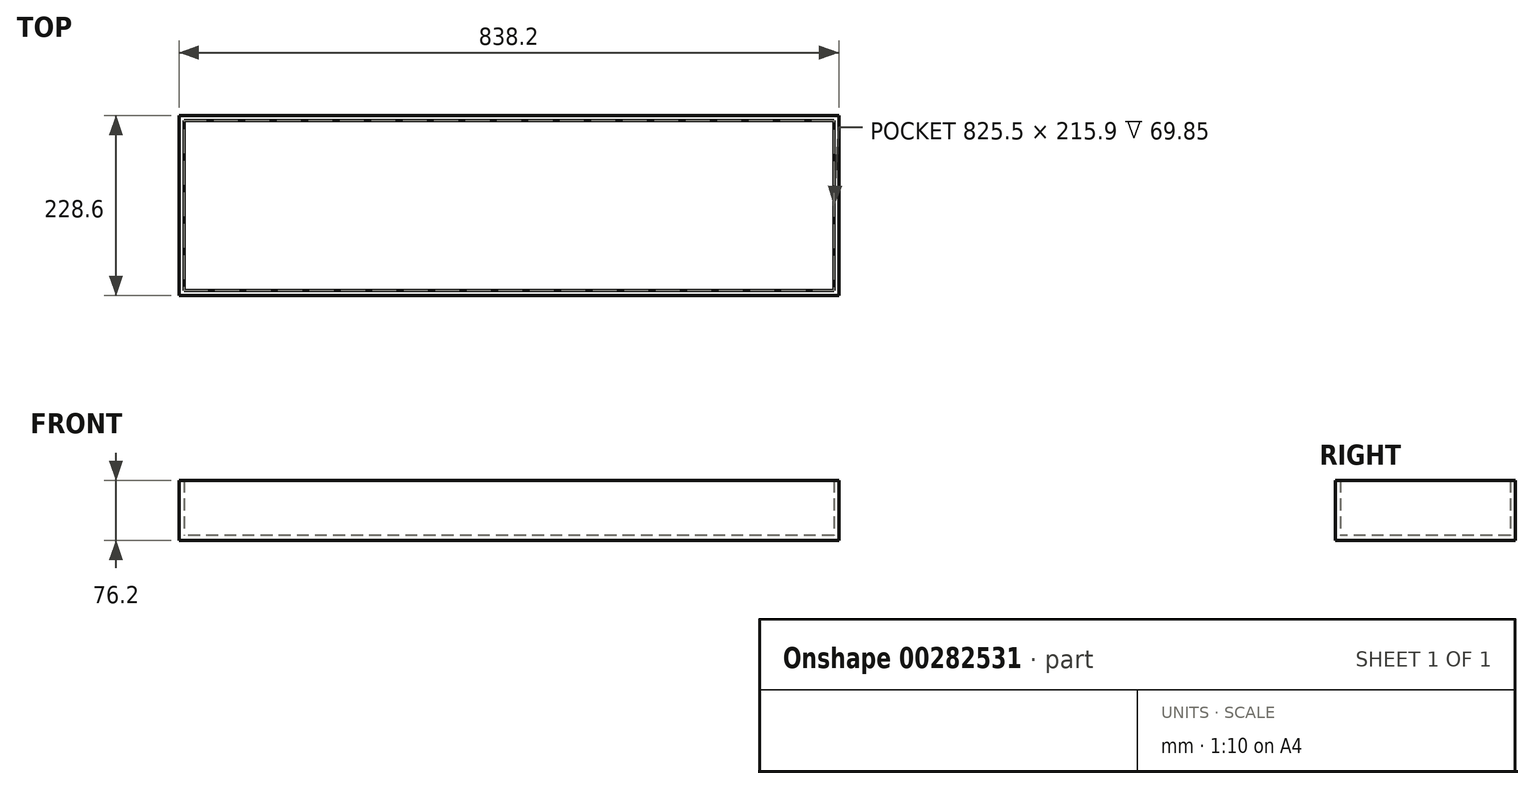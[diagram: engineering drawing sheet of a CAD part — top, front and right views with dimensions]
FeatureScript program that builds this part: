
annotation { "Feature Type Name" : "Feature", "Feature Type Description" : "" }
export const myFeature = defineFeature(function(context is Context, id is Id, definition is map)
    precondition{}
    {
        {
            var Q0;
            Q0=qCreatedBy(makeId("Top.planeOp"),FACE);
            var sketch = newSketch(context, id + "F0", { "sketchPlane" : qUnion([Q0])});
            skLineSegment(sketch, "E0.bottom", {"start": v(419.1, 114.3) * mm, "end": v(-419.1, 114.3) * mm});
            skLineSegment(sketch, "E0.top", {"start": v(419.1, -114.3) * mm, "end": v(-419.1, -114.3) * mm});
            skLineSegment(sketch, "E0.left", {"start": v(419.1, 114.3) * mm, "end": v(419.1, -114.3) * mm});
            skLineSegment(sketch, "E0.right", {"start": v(-419.1, 114.3) * mm, "end": v(-419.1, -114.3) * mm});
            skPoint(sketch, "E0.middle", {"position": v(0, 0) * mm});
            skSolve(sketch);
        }
        {
            var Q0;
            Q0=qSketchRegion(id+"F0",true);
            extrude(context, id + "F1", {"entities" : qUnion([Q0]), "endBound" : BoundingType.SYMMETRIC, "depth" : 76.2 * mm});
        }
        {
            var Q0;
            Q0=makeQuery(id+"F1.opExtrude","CAP_FACE",FACE,{"disambiguationData":[OSD([sQuery(id+"F0.wireOp",EDGE,"E0.bottom"),sQuery(id+"F0.wireOp",EDGE,"E0.top"),sQuery(id+"F0.wireOp",EDGE,"E0.left"),sQuery(id+"F0.wireOp",EDGE,"E0.right")])],"isStart":false});
            shell(context, id + "F2", {"entities" : qUnion([Q0]), "thickness" : 6.35 * mm});
        }
    });
